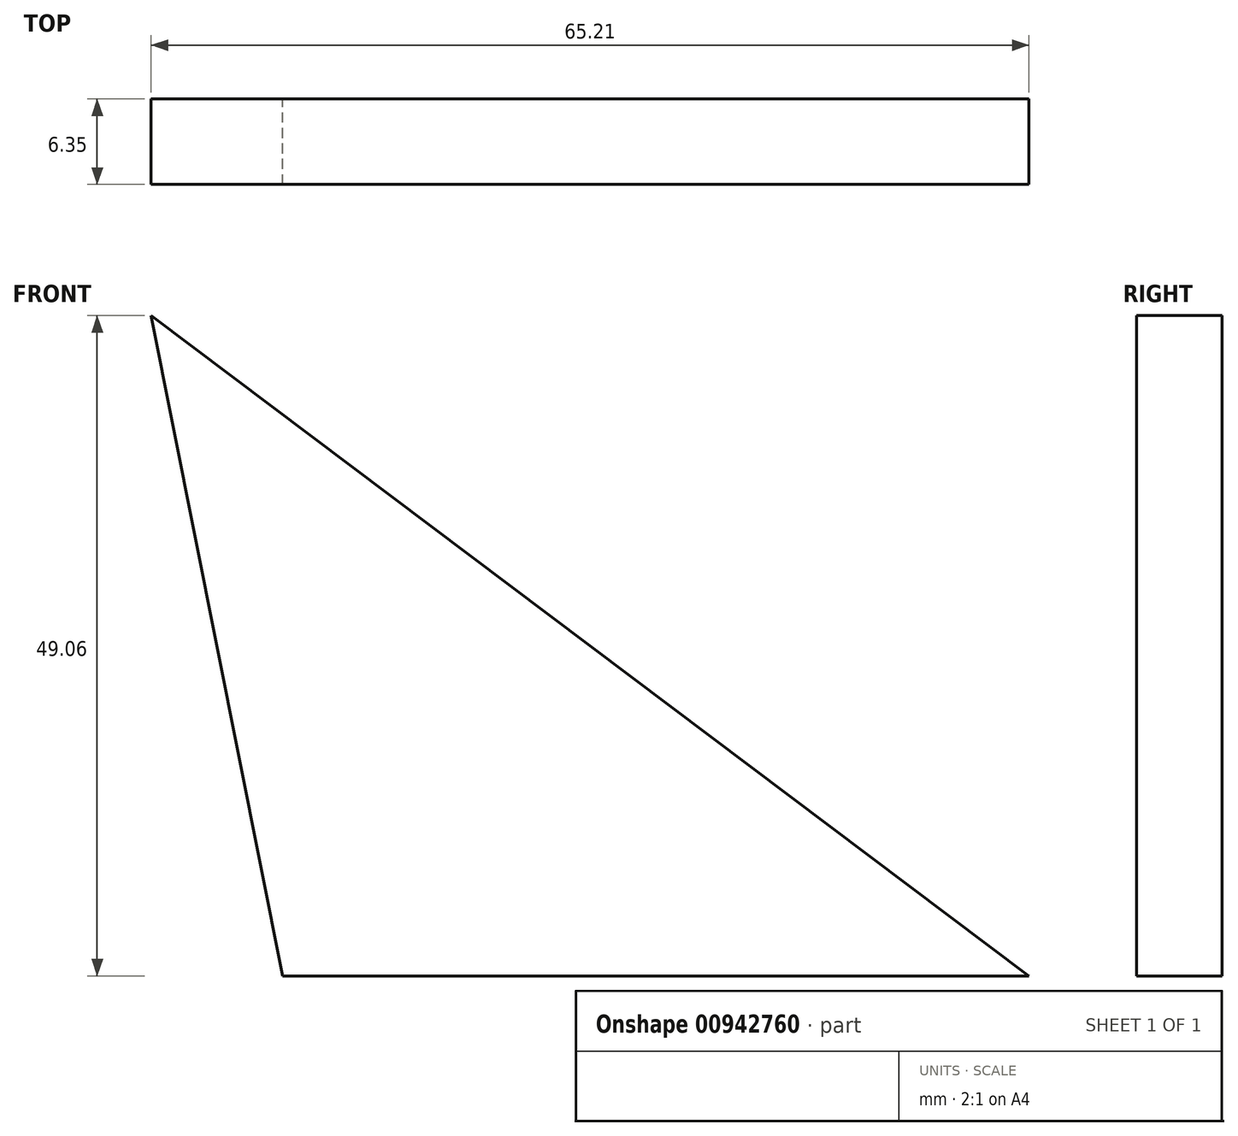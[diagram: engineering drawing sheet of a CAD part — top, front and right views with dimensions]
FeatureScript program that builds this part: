
annotation { "Feature Type Name" : "Feature", "Feature Type Description" : "" }
export const myFeature = defineFeature(function(context is Context, id is Id, definition is map)
    precondition{}
    {
        {
            var Q0;
            Q0=qCreatedBy(makeId("Front.planeOp"),FACE);
            var sketch = newSketch(context, id + "F0", { "sketchPlane" : qUnion([Q0])});
            skLineSegment(sketch, "E0", {"start": v(-65.2, 49.06) * mm, "end": v(0, 0) * mm});
            skLineSegment(sketch, "E1", {"start": v(0, 0) * mm, "end": v(-55.44, 0) * mm});
            skLineSegment(sketch, "E2", {"start": v(-55.44, 0) * mm, "end": v(-65.2, 49.06) * mm});
            skSolve(sketch);
        }
        {
            var Q0;
            Q0=makeQuery(id+"F0.imprint","IMPRINT",FACE,{"disambiguationData":[TD([[makeQuery(id+"F0.imprint","IMPRINT",EDGE,{"derivedFrom":sQuery(id+"F0.wireOp",EDGE,"E0")}),-1.0]])]});
            extrude(context, id + "F1", {"entities" : qUnion([Q0]), "depth" : 6.35 * mm, "offsetDistance" : 25.4 * mm});
        }
    });
